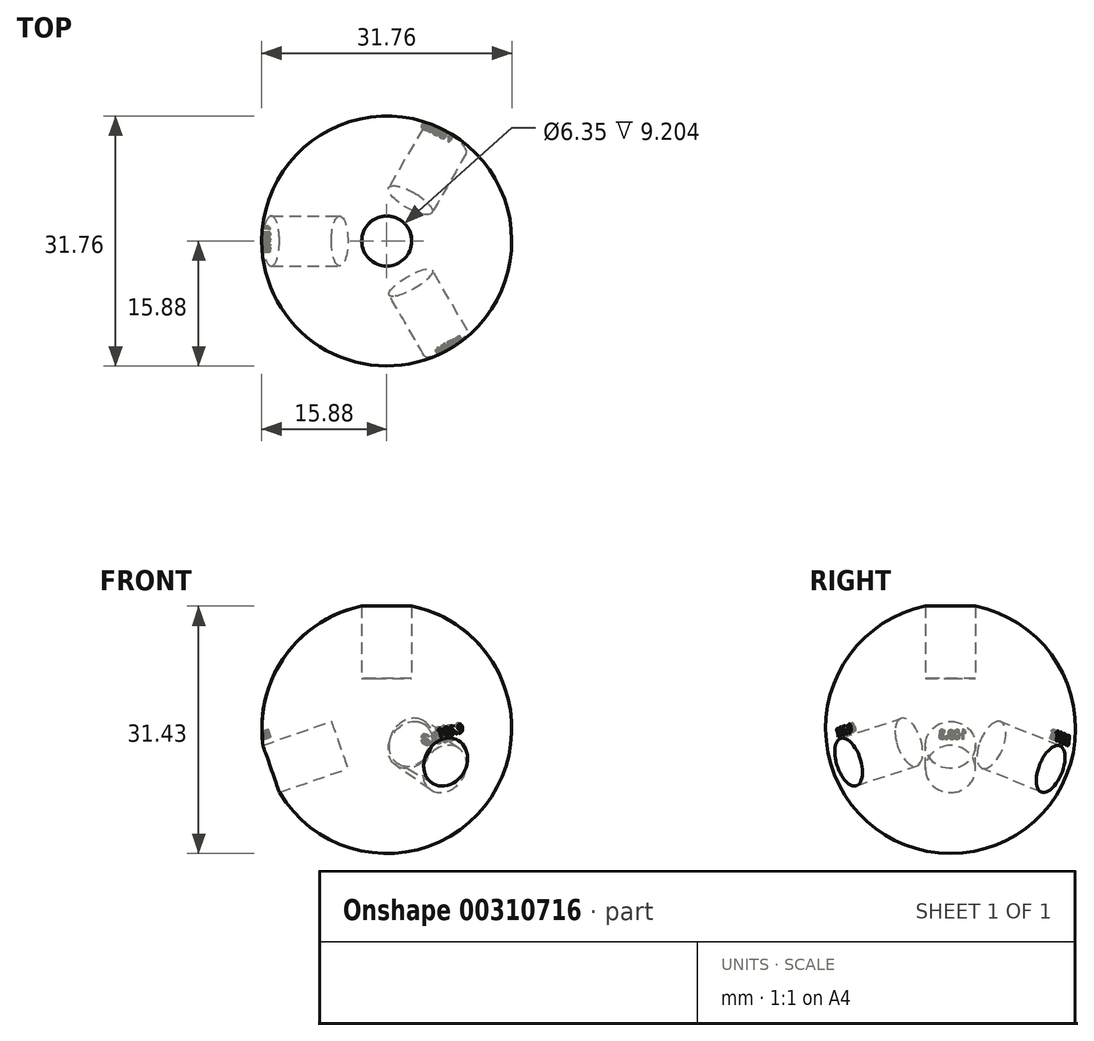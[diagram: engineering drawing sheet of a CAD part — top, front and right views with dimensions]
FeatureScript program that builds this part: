
annotation { "Feature Type Name" : "Feature", "Feature Type Description" : "" }
export const myFeature = defineFeature(function(context is Context, id is Id, definition is map)
    precondition{}
    {
        {
            var Q0;
            Q0=qCreatedBy(makeId("Front.planeOp"),FACE);
            var sketch = newSketch(context, id + "F0", { "sketchPlane" : qUnion([Q0])});
            skArc(sketch, "E0", {"start": v(0, 15.88) * mm, "mid": v(-15.88, 0) * mm, "end": v(0, -15.88) * mm});
            skLineSegment(sketch, "E1", {"start": v(0, 15.88) * mm, "end": v(0, -15.88) * mm});
            skLineSegment(sketch, "E2", {"start": v(0, 0) * mm, "end": v(60.07, 0) * mm, "construction": true});
            skLineSegment(sketch, "E3", {"start": v(60.07, 0) * mm, "end": v(0, 0) * mm, "construction": true});
            skLineSegment(sketch, "E4", {"start": v(0, 0) * mm, "end": v(0, 50.8) * mm, "construction": true});
            skSolve(sketch);
        }
        {
            var Q0;
            Q0=qCreatedBy(makeId("Top.planeOp"),FACE);
            var sketch = newSketch(context, id + "F1", { "sketchPlane" : qUnion([Q0])});
            skCircle(sketch, "E5", {"center": v(0, 0) * mm, "radius": 15.88 * mm});
            skLineSegment(sketch, "E6", {"start": v(0, 0) * mm, "end": v(0, -43.56) * mm, "construction": true});
            skSolve(sketch);
        }
        {
            var Q0;
            Q0=makeQuery(id+"F0.imprint","IMPRINT",FACE,{"disambiguationData":[TD([[makeQuery(id+"F0.imprint","IMPRINT",EDGE,{"derivedFrom":sQuery(id+"F0.wireOp",EDGE,"E0")}),1.0]])]});
            var Q1;
            Q1=sQuery(id+"F1.wireOp",EDGE,"E5");
            revolve(context, id + "F2", {"entities" : qUnion([Q0]), "axis" : qUnion([Q1]), "revolveType" : RevolveType.FULL});
        }
        {
            var Q0;
            Q0=qCreatedBy(makeId("Top.planeOp"),FACE);
            cPlane(context, id + "F3", {"entities" : qUnion([Q0]), "cplaneType" : CPlaneType.OFFSET, "offset" : 6.35 * mm, "width" : 152.4 * mm, "height" : 152.4 * mm});
        }
        {
            var Q0;
            Q0=qCreatedBy(id+"F3.planeOp",FACE);
            var sketch = newSketch(context, id + "F4", { "sketchPlane" : qUnion([Q0])});
            skCircle(sketch, "E7", {"center": v(0, 0) * mm, "radius": 3.18 * mm});
            skSolve(sketch);
        }
        {
            var Q0;
            Q0=makeQuery(id+"F4.imprint","IMPRINT",FACE,{"disambiguationData":[TD([[makeQuery(id+"F4.imprint","IMPRINT",EDGE,{"derivedFrom":sQuery(id+"F4.wireOp",EDGE,"E7")}),1.0]])]});
            extrude(context, id + "F5", {"entities" : qUnion([Q0]), "depth" : 50.8 * mm});
        }
        {
            var Q0;
            Q0=qCreatedBy(makeId("Front.planeOp"),FACE);
            var sketch = newSketch(context, id + "F6", { "sketchPlane" : qUnion([Q0])});
            skLineSegment(sketch, "E8", {"start": v(0, 0) * mm, "end": v(0, -31.9) * mm});
            skSolve(sketch);
        }
        {
            var Q0;
            Q0=makeQuery(id+"F5.opExtrude","SWEPT_BODY",BODY,{"disambiguationData":[OSD([sQuery(id+"F4.wireOp",EDGE,"E7")])]});
            var Q1;
            Q1=makeQuery(id+"F5.opExtrude","CAP_EDGE",EDGE,{"disambiguationData":[OSD([sQuery(id+"F4.wireOp",EDGE,"E7")])],"isStart":false});
            var Q2;
            Q2=makeQuery(id+"F5.opExtrude","SWEPT_FACE",FACE,{"disambiguationData":[OSD([sQuery(id+"F4.wireOp",EDGE,"E7")])]});
            transform(context, id + "F7", {"entities" : qUnion([Q0]), "transformType" : TransformType.ROTATION, "transformAxis" : qUnion([Q2]), "angle" : 120 * degree, "makeCopy" : true});
        }
        {
            var Q0;
            Q0=makeQuery(id+"F5.opExtrude","SWEPT_BODY",BODY,{"disambiguationData":[OSD([sQuery(id+"F4.wireOp",EDGE,"E7")])]});
            var Q1;
            Q1=makeQuery(id+"F2.opRevolve","SWEPT_BODY",BODY,{"disambiguationData":[OSD([sQuery(id+"F0.wireOp",EDGE,"E0"),sQuery(id+"F0.wireOp",EDGE,"E1")])]});
            var Q2;
            Q2=sQuery(id+"F1.wireOp",EDGE,"E6");
            transform(context, id + "F8", {"entities" : qUnion([Q0, Q1]), "transformType" : TransformType.ROTATION, "transformAxis" : qUnion([Q2]), "angle" : 109.3 * degree, "makeCopy" : false});
        }
        {
            var Q0;
            Q0=makeQuery(id+"F5.opExtrude","SWEPT_BODY",BODY,{"disambiguationData":[OSD([sQuery(id+"F4.wireOp",EDGE,"E7")])]});
            var Q1;
            Q1=sQuery(id+"F6.wireOp",EDGE,"E8");
            transform(context, id + "F9", {"entities" : qUnion([Q0]), "transformType" : TransformType.ROTATION, "transformAxis" : qUnion([Q1]), "angle" : 120 * degree, "makeCopy" : true});
        }
        {
            var Q0;
            Q0=makeQuery(id+"F7.opPattern","COPY",BODY,{"derivedFrom":makeQuery(id+"F5.opExtrude","SWEPT_BODY",BODY,{"disambiguationData":[OSD([sQuery(id+"F4.wireOp",EDGE,"E7")])]}),"instanceName":"1"});
            var Q1;
            Q1=sQuery(id+"F1.wireOp",EDGE,"E6");
            transform(context, id + "F10", {"entities" : qUnion([Q0]), "transformType" : TransformType.ROTATION, "transformAxis" : qUnion([Q1]), "angle" : 105.9 * degree, "oppositeDirection" : true, "makeCopy" : true});
        }
        {
            var Q0;
            Q0=makeQuery(id+"F10.opPattern","COPY",BODY,{"derivedFrom":makeQuery(id+"F7.opPattern","COPY",BODY,{"derivedFrom":makeQuery(id+"F5.opExtrude","SWEPT_BODY",BODY,{"disambiguationData":[OSD([sQuery(id+"F4.wireOp",EDGE,"E7")])]}),"instanceName":"1"}),"instanceName":"1"});
            var Q1;
            Q1=sQuery(id+"F0.wireOp",EDGE,"E4");
            transform(context, id + "F11", {"entities" : qUnion([Q0]), "transformType" : TransformType.ROTATION, "transformAxis" : qUnion([Q1]), "angle" : 60 * degree, "oppositeDirection" : true, "makeCopy" : false});
        }
        {
            var Q0;
            Q0=makeQuery(id+"F5.opExtrude","CAP_FACE",FACE,{"disambiguationData":[OSD([sQuery(id+"F4.wireOp",EDGE,"E7")])],"isStart":false});
            cPlane(context, id + "F12", {"entities" : qUnion([Q0]), "cplaneType" : CPlaneType.OFFSET, "offset" : 31.75 * mm, "oppositeDirection" : true, "width" : 152.4 * mm, "height" : 152.4 * mm});
        }
        {
            var Q0;
            Q0=qCreatedBy(id+"F12.planeOp",FACE);
            var sketch = newSketch(context, id + "F13", { "sketchPlane" : qUnion([Q0])});
            skText(sketch, "E9", { "text": "109.3\n", "fontName": "OpenSans-Regular.ttf"});
            const initialGuessF13  = {"E9": [-0.002, 0.00389, 1, 0, 0.00098]};
            skSetInitialGuess(sketch, initialGuessF13);
            skSolve(sketch);
        }
        {
            var Q0;
            Q0=qSketchRegion(id+"F13",true);
            extrude(context, id + "F14", {"entities" : qUnion([Q0]), "operationType" : NewBodyOperationType.REMOVE, "oppositeDirection" : true, "depth" : 11.1 * mm});
        }
        {
            var Q0;
            Q0=makeQuery(id+"F9.opPattern","COPY",FACE,{"derivedFrom":makeQuery(id+"F5.opExtrude","CAP_FACE",FACE,{"disambiguationData":[OSD([sQuery(id+"F4.wireOp",EDGE,"E7")])],"isStart":false}),"instanceName":"1"});
            cPlane(context, id + "F15", {"entities" : qUnion([Q0]), "cplaneType" : CPlaneType.OFFSET, "offset" : 38.1 * mm, "oppositeDirection" : true, "width" : 152.4 * mm, "height" : 152.4 * mm});
        }
        {
            var Q0;
            Q0=qCreatedBy(id+"F15.planeOp",FACE);
            var sketch = newSketch(context, id + "F16", { "sketchPlane" : qUnion([Q0])});
            skText(sketch, "E10", { "text": "109.3\n", "fontName": "OpenSans-Regular.ttf"});
            const initialGuessF16  = {"E10": [-0.00171, 0.00356, 1, 0, 0.00128]};
            skSetInitialGuess(sketch, initialGuessF16);
            skSolve(sketch);
        }
        {
            var Q0;
            Q0 = qSketchRegion(id + "F16", true);
            extrude(context, id + "F17", {"entities" : qUnion([Q0]), "operationType" : NewBodyOperationType.REMOVE, "oppositeDirection" : true, "depth" : 4.62 * mm});
        }
        {
            var Q0;
            Q0=makeQuery(id+"F10.opPattern","COPY",FACE,{"derivedFrom":makeQuery(id+"F7.opPattern","COPY",FACE,{"derivedFrom":makeQuery(id+"F5.opExtrude","CAP_FACE",FACE,{"disambiguationData":[OSD([sQuery(id+"F4.wireOp",EDGE,"E7")])],"isStart":false}),"instanceName":"1"}),"instanceName":"1"});
            cPlane(context, id + "F18", {"entities" : qUnion([Q0]), "cplaneType" : CPlaneType.OFFSET, "offset" : 38.1 * mm, "oppositeDirection" : true, "width" : 152.4 * mm, "height" : 152.4 * mm});
        }
        {
            var Q0;
            Q0=qCreatedBy(id+"F18.planeOp",FACE);
            var sketch = newSketch(context, id + "F19", { "sketchPlane" : qUnion([Q0])});
            skText(sketch, "E11", { "text": "105.9\n", "fontName": "OpenSans-Regular.ttf"});
            const initialGuessF19  = {"E11": [-0.00111, 0.00346, 1, 0, 0.00109]};
            skSetInitialGuess(sketch, initialGuessF19);
            skSolve(sketch);
        }
        {
            var Q0;
            Q0 = qSketchRegion(id + "F19", true);
            extrude(context, id + "F20", {"entities" : qUnion([Q0]), "operationType" : NewBodyOperationType.REMOVE, "oppositeDirection" : true, "depth" : 4.5 * mm});
        }
        {
            var Q0;
            Q0=makeQuery(id+"F10.opPattern","COPY",BODY,{"derivedFrom":makeQuery(id+"F7.opPattern","COPY",BODY,{"derivedFrom":makeQuery(id+"F5.opExtrude","SWEPT_BODY",BODY,{"disambiguationData":[OSD([sQuery(id+"F4.wireOp",EDGE,"E7")])]}),"instanceName":"1"}),"instanceName":"1"});
            var Q1;
            Q1=makeQuery(id+"F5.opExtrude","SWEPT_BODY",BODY,{"disambiguationData":[OSD([sQuery(id+"F4.wireOp",EDGE,"E7")])]});
            var Q2;
            Q2=makeQuery(id+"F9.opPattern","COPY",BODY,{"derivedFrom":makeQuery(id+"F5.opExtrude","SWEPT_BODY",BODY,{"disambiguationData":[OSD([sQuery(id+"F4.wireOp",EDGE,"E7")])]}),"instanceName":"1"});
            var Q3;
            Q3=makeQuery(id+"F7.opPattern","COPY",BODY,{"derivedFrom":makeQuery(id+"F5.opExtrude","SWEPT_BODY",BODY,{"disambiguationData":[OSD([sQuery(id+"F4.wireOp",EDGE,"E7")])]}),"instanceName":"1"});
            var Q4;
            Q4=makeQuery(id+"F2.opRevolve","SWEPT_BODY",BODY,{"disambiguationData":[OSD([sQuery(id+"F0.wireOp",EDGE,"E0"),sQuery(id+"F0.wireOp",EDGE,"E1")])]});
            booleanBodies(context, id + "F21", {"operationType" : BooleanOperationType.SUBTRACTION, "tools" : qUnion([Q0, Q1, Q2, Q3]), "targets" : qUnion([Q4])});
        }
    });
